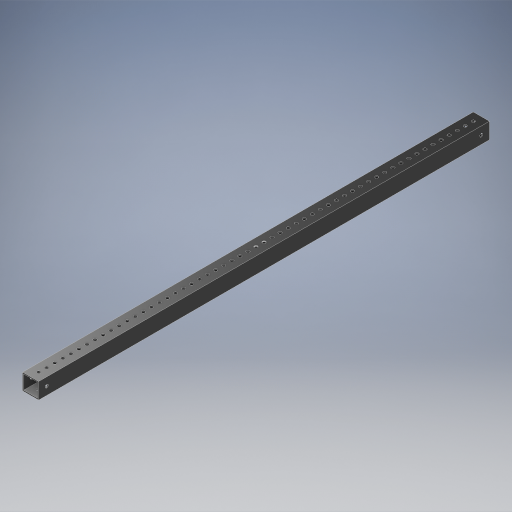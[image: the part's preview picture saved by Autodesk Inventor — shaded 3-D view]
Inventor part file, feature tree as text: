
AUTODESK INVENTOR PART (.ipt)
format: ipt  version: 2024.2 (Build 282272000, 272)  size: 861,184 bytes
history: native  units: in
note: dims shown in document units (in); Inventor stores cm internally (conversion verified against a paired STEP export)
features: other x13, extrude x9, hole x3, pattern_linear x3, mirror x3, sheet_metal_op x1, plane x1
ambient origin geometry x8: Origin, YZ Plane, XZ Plane, XY Plane, X Axis, Y Axis, Z Axis, Center Point
bodies: Solid1 (feature_tree)
feature tree (33):
  other  "Blocks"
  other  "Base Sketch"
  extrude  "Base"  Depth=1.0in
  extrude  "MAX Corner"  Depth=1.0in
  extrude  "MAX Corner Cut"  Depth=0.0625in
  extrude  "Scribe Lines"  Depth=0.0625in
  other  "Side Middle"
  other  "Top Middle"
  other  "Side Holes Sketch"
  hole  "Top Side Hole"  [1 undecoded]
  hole  "Mid Side Hole"  [1 undecoded]
  hole  "Btm Side Hole"  [1 undecoded]
  pattern_linear  "Side Holes"  Spacing1=0.04in  [1 undecoded]
  mirror  "Side Mirror"
  extrude  "MAXTube Hole"  Depth=0.04in
  extrude  "MAXTube Outside"  Depth=28.0in
  pattern_linear  "MAXTube Pattern"  Spacing1=0.0in  [1 undecoded]
  mirror  "MAXTube Mirror"
  extrude  "Left Top Hole"  Depth=28.0in
  extrude  "Mid Top Hole"  TaperAngle=0.0deg  [1 undecoded]
  extrude  "Right Top Hole"  TaperAngle=0.0deg  [1 undecoded]
  pattern_linear  "Top Holes"  Spacing1=0.005in  [1 undecoded]
  mirror  "Top Mirror"
  sheet_metal_op  "Corner"
  other  "MAXTube"
  plane  "Work Plane3"
  other  "Corner:5"
  other  "Corner:6"
  other  "Corner:7"
  other  "Corner:8"
  other  "MAXTube:1"
  other  "MAXTube:2"
  other  "MAXTube:3"
note: 8 required parameter values undecoded (feature->parameter linkage not recoverable at this tier; creation-order binding heuristic only, values carry confidence <= 0.55)
